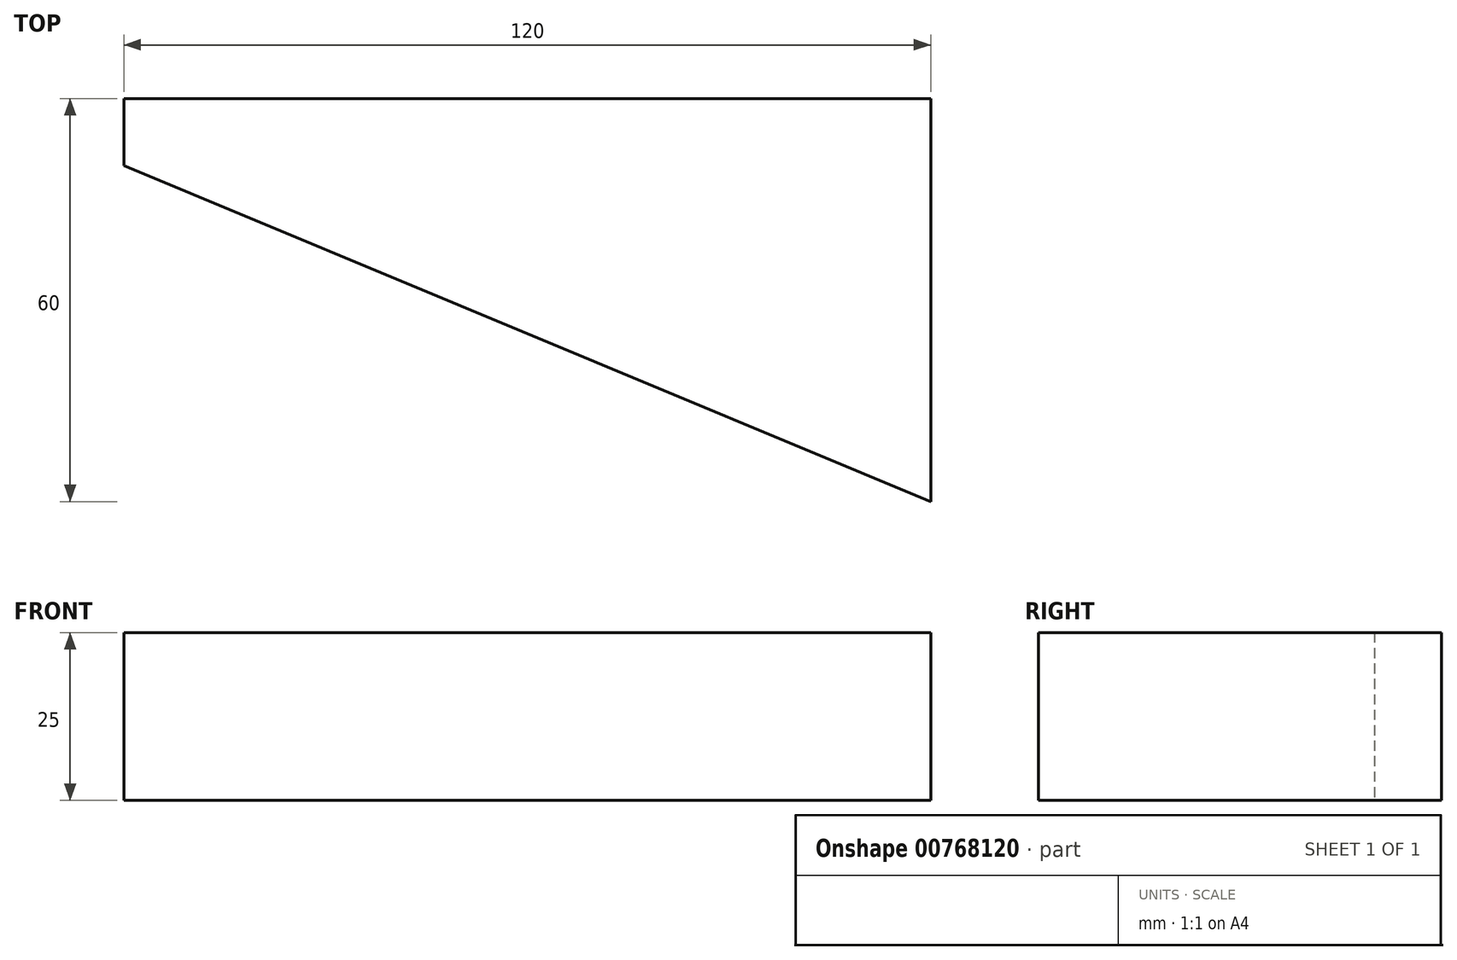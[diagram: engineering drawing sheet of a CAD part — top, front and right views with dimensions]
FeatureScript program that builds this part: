
annotation { "Feature Type Name" : "Feature", "Feature Type Description" : "" }
export const myFeature = defineFeature(function(context is Context, id is Id, definition is map)
    precondition{}
    {
        {
            var Q0;
            Q0=qCreatedBy(makeId("Top.planeOp"),FACE);
            var sketch = newSketch(context, id + "F0", { "sketchPlane" : qUnion([Q0])});
            skLineSegment(sketch, "E0.bottom", {"start": v(60, 30) * mm, "end": v(-60, 30) * mm});
            skLineSegment(sketch, "E0.left", {"start": v(60, 30) * mm, "end": v(60, -30) * mm});
            skPoint(sketch, "E0.middle", {"position": v(0, 0) * mm});
            skLineSegment(sketch, "E1", {"start": v(60, -30) * mm, "end": v(-60, 30) * mm});
            skPoint(sketch, "E0.top.end.orphan", {"position": v(-60, -30) * mm});
            skLineSegment(sketch, "E2", {"start": v(-60, 20) * mm, "end": v(-60, 30) * mm});
            skLineSegment(sketch, "E3", {"start": v(60, -30) * mm, "end": v(-60, 20) * mm});
            skSolve(sketch);
        }
        {
            var Q0;
            Q0=makeQuery(id+"F0.imprint","IMPRINT",FACE,{"disambiguationData":[TD([[makeQuery(id+"F0.imprint","IMPRINT",EDGE,{"derivedFrom":sQuery(id+"F0.wireOp",EDGE,"E0.bottom")}),1.0]])]});
            var Q1;
            Q1=makeQuery(id+"F0.imprint","IMPRINT",FACE,{"disambiguationData":[TD([[makeQuery(id+"F0.imprint","IMPRINT",EDGE,{"derivedFrom":sQuery(id+"F0.wireOp",EDGE,"E1")}),1.0]])]});
            extrude(context, id + "F1", {"entities" : qUnion([Q0, Q1]), "depth" : 25 * mm, "offsetDistance" : 25 * mm});
        }
    });
